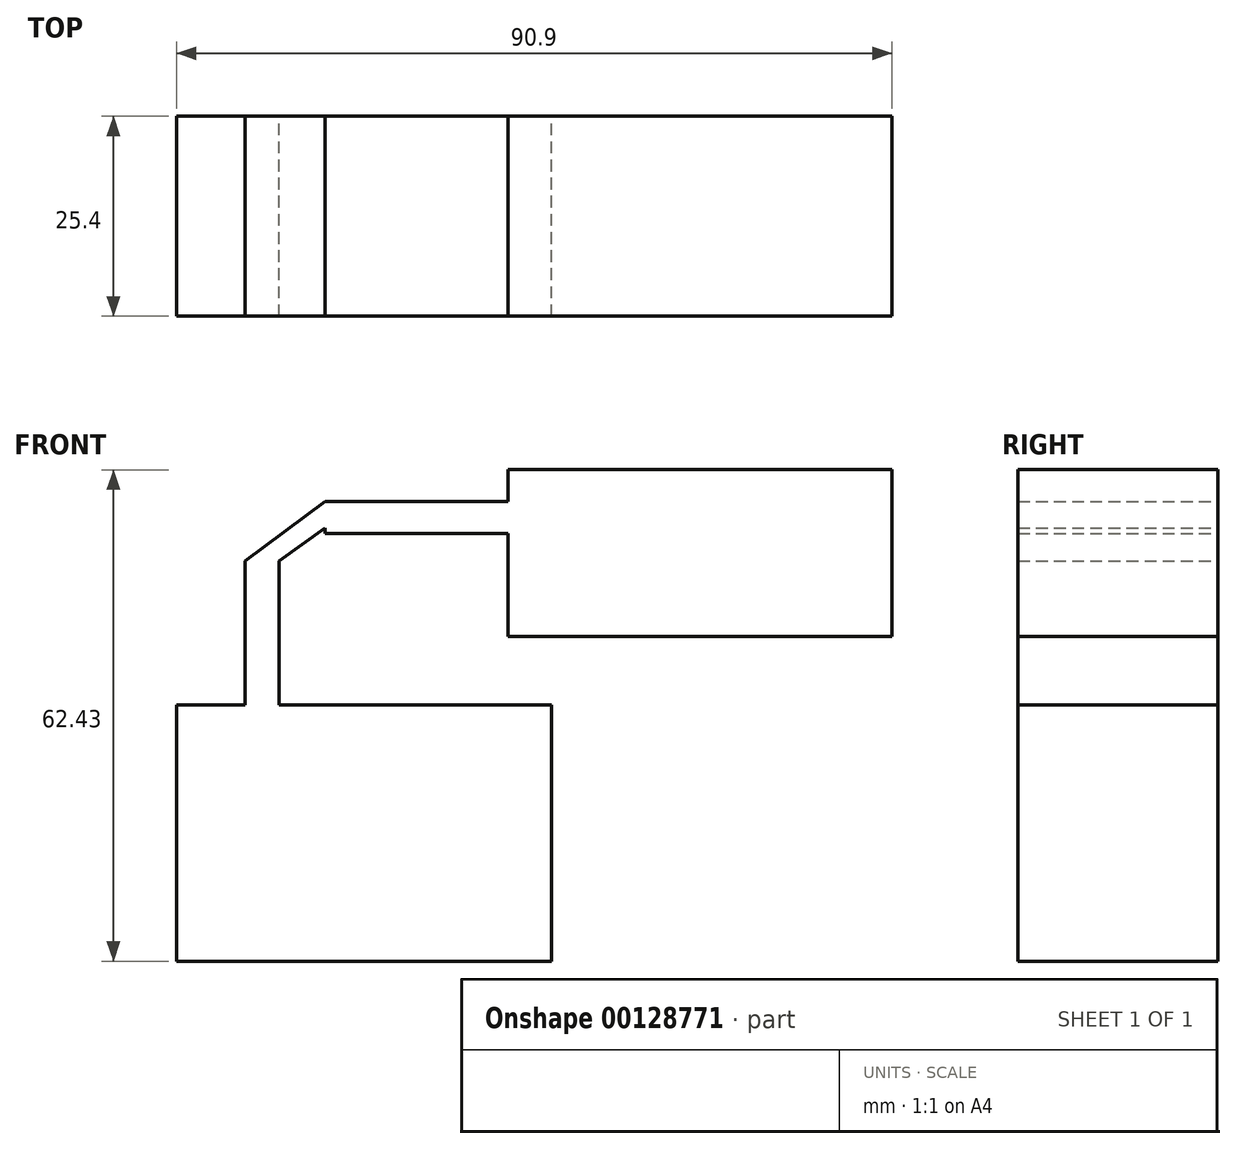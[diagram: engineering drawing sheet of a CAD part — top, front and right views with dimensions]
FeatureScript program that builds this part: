
annotation { "Feature Type Name" : "Feature", "Feature Type Description" : "" }
export const myFeature = defineFeature(function(context is Context, id is Id, definition is map)
    precondition{}
    {
        {
            var Q0;
            Q0=qCreatedBy(makeId("Front.planeOp"),FACE);
            var sketch = newSketch(context, id + "F0", { "sketchPlane" : qUnion([Q0])});
            skLineSegment(sketch, "E0.bottom", {"start": v(-42.11, 11.76) * mm, "end": v(5.52, 11.76) * mm});
            skLineSegment(sketch, "E0.top", {"start": v(-42.11, -20.76) * mm, "end": v(5.52, -20.76) * mm});
            skLineSegment(sketch, "E0.left", {"start": v(-42.11, 11.76) * mm, "end": v(-42.11, -20.76) * mm});
            skLineSegment(sketch, "E0.right", {"start": v(5.52, 11.76) * mm, "end": v(5.52, -20.76) * mm});
            skLineSegment(sketch, "E1.bottom", {"start": v(0, 41.67) * mm, "end": v(48.8, 41.67) * mm});
            skLineSegment(sketch, "E1.top", {"start": v(0, 20.47) * mm, "end": v(48.8, 20.47) * mm});
            skLineSegment(sketch, "E1.left", {"start": v(0, 41.67) * mm, "end": v(0, 20.47) * mm});
            skLineSegment(sketch, "E1.right", {"start": v(48.8, 41.67) * mm, "end": v(48.8, 20.47) * mm});
            skLineSegment(sketch, "E2.bottom", {"start": v(-33.4, 9.15) * mm, "end": v(-29.04, 9.15) * mm});
            skLineSegment(sketch, "E2.top", {"start": v(-33.4, 23.38) * mm, "end": v(-29.04, 23.38) * mm});
            skLineSegment(sketch, "E2.left", {"start": v(-33.4, 9.15) * mm, "end": v(-33.4, 23.38) * mm});
            skLineSegment(sketch, "E2.right", {"start": v(-29.04, 9.15) * mm, "end": v(-29.04, 23.38) * mm});
            skLineSegment(sketch, "E3.top", {"start": v(-33.4, 30.06) * mm, "end": v(-29.04, 30.06) * mm});
            skLineSegment(sketch, "E3.left", {"start": v(-33.4, 23.38) * mm, "end": v(-33.4, 30.06) * mm});
            skLineSegment(sketch, "E3.right", {"start": v(-29.04, 23.38) * mm, "end": v(-29.04, 30.06) * mm});
            skLineSegment(sketch, "E4", {"start": v(-33.4, 30.06) * mm, "end": v(-23.23, 37.6) * mm});
            skLineSegment(sketch, "E5", {"start": v(-29.04, 30.06) * mm, "end": v(-18.59, 37.6) * mm});
            skLineSegment(sketch, "E6.bottom", {"start": v(-23.23, 37.6) * mm, "end": v(8.13, 37.6) * mm});
            skLineSegment(sketch, "E6.top", {"start": v(-23.23, 33.54) * mm, "end": v(8.13, 33.54) * mm});
            skLineSegment(sketch, "E6.left", {"start": v(-23.23, 37.6) * mm, "end": v(-23.23, 33.54) * mm});
            skLineSegment(sketch, "E6.right", {"start": v(8.13, 37.6) * mm, "end": v(8.13, 33.54) * mm});
            skSolve(sketch);
        }
        {
            var Q0;
            {var subQ5=sQuery(id+"F0.wireOp",EDGE,"E2.top");Q0=makeQuery(id+"F0.imprint","IMPRINT",FACE,{"disambiguationData":[TD([[makeQuery(id+"F0.imprint","IMPRINT",EDGE,{"derivedFrom":subQ5}),-1.0]])]});}
            var Q1;
            Q1=makeQuery(id+"F0.imprint","IMPRINT",FACE,{"disambiguationData":[TD([[makeQuery(id+"F0.imprint","IMPRINT",EDGE,{"derivedFrom":sQuery(id+"F0.wireOp",EDGE,"E0.top")}),1.0]])]});
            var Q2;
            {var subQ4=sQuery(id+"F0.wireOp",EDGE,"E1.bottom");Q2=makeQuery(id+"F0.imprint","IMPRINT",FACE,{"disambiguationData":[TD([[makeQuery(id+"F0.imprint","IMPRINT",EDGE,{"derivedFrom":subQ4}),-1.0]])]});}
            var Q3;
            {var subQ3=sQuery(id+"F0.wireOp",EDGE,"E1.left");var subQ5=sQuery(id+"F0.wireOp",EDGE,"E6.bottom");var subQ9=makeQuery(id+"F0.imprint","INTERSECT",VERTEX,{"derivedFrom":[subQ3,subQ5]});Q3=makeQuery(id+"F0.imprint","IMPRINT",FACE,{"disambiguationData":[TD([[makeQuery(id+"F0.imprint","IMPRINT",EDGE,{"disambiguationData":[TD([[subQ9,-1.0]])],"derivedFrom":subQ3}),-1.0]])]});}
            var Q4;
            Q4=makeQuery(id+"F0.imprint","IMPRINT",FACE,{"disambiguationData":[TD([[makeQuery(id+"F0.imprint","IMPRINT",EDGE,{"derivedFrom":sQuery(id+"F0.wireOp",EDGE,"E2.top")}),1.0]])]});
            var Q5;
            {var subQ5=sQuery(id+"F0.wireOp",EDGE,"E6.right");Q5=makeQuery(id+"F0.imprint","IMPRINT",FACE,{"disambiguationData":[TD([[makeQuery(id+"F0.imprint","IMPRINT",EDGE,{"derivedFrom":subQ5}),-1.0]])]});}
            var Q6;
            {var subQ0=sQuery(id+"F0.wireOp",EDGE,"E3.top");Q6=makeQuery(id+"F0.imprint","IMPRINT",FACE,{"disambiguationData":[TD([[makeQuery(id+"F0.imprint","IMPRINT",EDGE,{"derivedFrom":subQ0}),1.0]])]});}
            var Q7;
            {var subQ5=sQuery(id+"F0.wireOp",EDGE,"E2.bottom");Q7=makeQuery(id+"F0.imprint","IMPRINT",FACE,{"disambiguationData":[TD([[makeQuery(id+"F0.imprint","IMPRINT",EDGE,{"derivedFrom":subQ5}),1.0]])]});}
            var Q8;
            {var subQ0=sQuery(id+"F0.wireOp",EDGE,"E6.bottom");var subQ1=sQuery(id+"F0.wireOp",EDGE,"E5");var subQ2=makeQuery(id+"F0.imprint","INTERSECT",VERTEX,{"derivedFrom":[subQ1,subQ0]});Q8=makeQuery(id+"F0.imprint","IMPRINT",FACE,{"disambiguationData":[TD([[makeQuery(id+"F0.imprint","IMPRINT",EDGE,{"disambiguationData":[TD([[subQ2,1.0]])],"derivedFrom":subQ1}),1.0]])]});}
            extrude(context, id + "F1", {"entities" : qUnion([Q0, Q1, Q2, Q3, Q4, Q5, Q6, Q7, Q8]), "depth" : 25.4 * mm});
        }
    });
